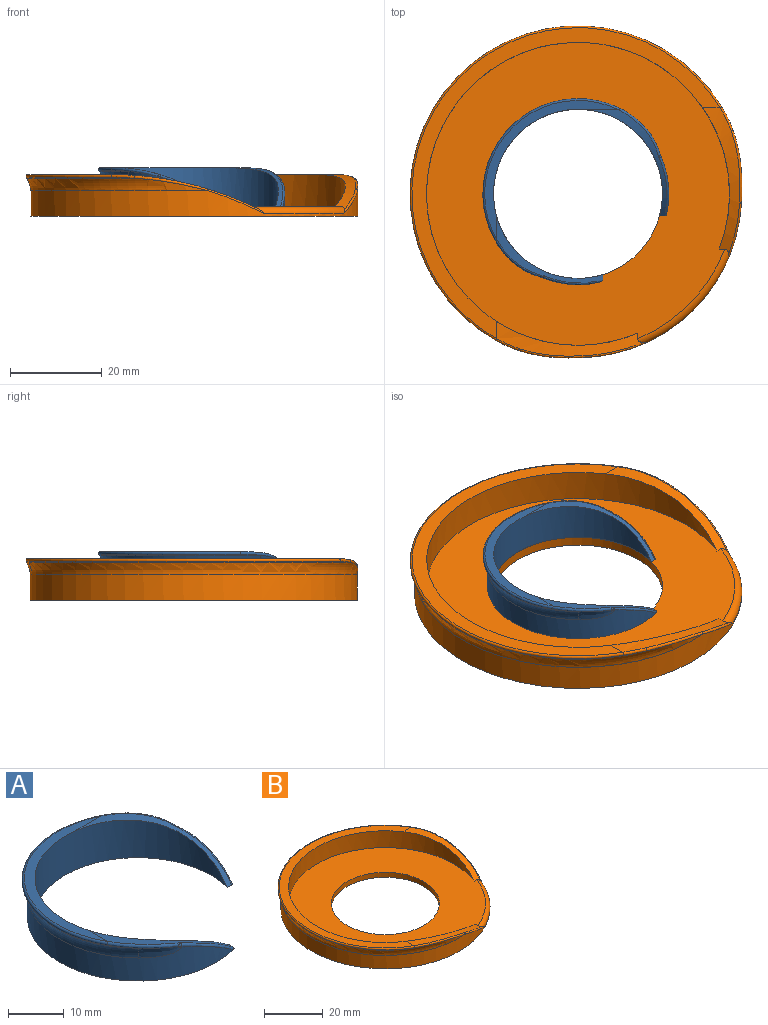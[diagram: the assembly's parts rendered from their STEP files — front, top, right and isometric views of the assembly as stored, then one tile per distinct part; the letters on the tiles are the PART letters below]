
ASSEMBLY  parts=2 mates=1
PART A: 17 faces, bbox 43x43x10.5 mm
  f0: cylinder r=19.8mm len=39.6mm, axis (0,0,1), area 484.6mm2, adj f1,f7,f9,f13,f14,f15
  f1: plane 39.72x39.72mm, normal (0,0,-1), area 138.9mm2, adj f0,f4,f5,f6,f7,f9
  f2: plane 30.36x29.2mm, normal (0,0,1), area 85.9mm2, adj f4,f5,f6,f10
  f3: cone r=21.07mm half-angle=32deg, axis (0,0,1), area 12mm2, adj f8,f10,f11,f14
  f4: cylinder r=18.41mm len=36.83mm, axis (0,0,1), area 568.8mm2, adj f1,f2,f5,f6
  f5: cylinder r=35.56mm len=23.11mm, axis (0,-1,0), area 39.2mm2, adj f1,f2,f4,f9,f11
  f6: cylinder r=35.56mm len=23.11mm, axis (-1,0,0), area 41.2mm2, adj f1,f2,f4,f7,f8
  f7: bspline ~15.72x8.88mm, area 9.5mm2, adj f0,f1,f6,f16
  f8: bspline ~14.08x12mm, area 12.1mm2, adj f3,f6,f10,f15,f16
  f9: bspline ~15.62x9.06mm, area 9.3mm2, adj f0,f1,f5,f12
  f10: torus R=20.34mm, axis (0,0,1), area 45.3mm2, adj f2,f3,f8,f11
  f11: bspline ~13.01x10.89mm, area 11.6mm2, adj f3,f5,f10,f12,f13
  f12: bspline ~0.69x0.6mm, area 0.2mm2, adj f9,f11,f13
  f13: bspline ~8.76x5.95mm, area 16.4mm2, adj f0,f11,f12,f14
  f14: torus R=24.88mm, axis (0,0,1), area 177.3mm2, adj f0,f3,f13,f15
  f15: bspline ~8.66x6.36mm, area 16.8mm2, adj f0,f8,f14,f16
  f16: bspline ~0.68x0.6mm, area 0.2mm2, adj f7,f8,f15
PART B: 18 faces, bbox 80.4x80.4x10.6 mm
  f0: cylinder r=35.67mm len=71.35mm, axis (0,0,1), area 1062.6mm2, adj f3,f8,f9,f13,f16
  f1: plane 67.76x67.18mm, normal (0,0,1), area 397.6mm2, adj f5,f6,f7,f12
  f2: cone r=36.94mm half-angle=32deg, axis (0,0,1), area 28.6mm2, adj f8,f11,f12,f14
  f3: plane 71.35x71.35mm, normal (0,0,-1), area 2932.8mm2, adj f0,f17
  f4: plane 66.04x66.04mm, normal (0,0,1), area 2390.6mm2, adj f5,f6,f7,f16,f17
  f5: cylinder r=33.02mm len=66.04mm, axis (0,0,1), area 1045mm2, adj f1,f4,f6,f7
  f6: cylinder r=71.12mm len=31.94mm, axis (-1,0,0), area 82.7mm2, adj f1,f4,f5,f13,f14,f15,f16
  f7: cylinder r=71.12mm len=31.95mm, axis (0,1,0), area 82.4mm2, adj f1,f4,f5,f9,f10,f11,f16
  f8: torus R=40.75mm, axis (0,0,1), area 448.7mm2, adj f0,f2,f10,f15
  f9: bspline ~19.46x8.28mm, area 7.9mm2, adj f0,f7,f10,f16
  f10: bspline ~23.57x4.6mm, area 12.7mm2, adj f7,f8,f9,f11
  f11: bspline ~11.65x5.94mm, area 4.8mm2, adj f2,f7,f10,f12
  f12: torus R=36.21mm, axis (0,0,1), area 115.4mm2, adj f1,f2,f11,f14
  f13: bspline ~19.58x8.35mm, area 7.9mm2, adj f0,f6,f15,f16
  f14: bspline ~11.57x6.31mm, area 4.9mm2, adj f2,f6,f12,f15
  f15: bspline ~23.44x5.12mm, area 12.8mm2, adj f6,f8,f13,f14
  f16: torus R=34.15mm, axis (0,0,1), area 65.7mm2, adj f0,f4,f6,f7,f9,f13
  f17: cylinder r=18.41mm len=36.83mm, axis (0,0,1), area 241mm2, adj f3,f4
PLACE A t=(-3.75,14.83,5.83)mm
PLACE B t=(-3.75,-1.04,3.75)mm
MATE fastened A.f4 <-> B.f0  axis (0,0,-1) through (-3.75,19.98,5.83)mm
